# Revit family: ВКДВ_К2
name_source: partatom
category: Оборудование
units: mm (PartAtom-declared; Revit-internal decimal feet)

## family parameters
Всегда вертикально = Да
Классификация = Нет
На основе рабочей плоскости = Нет
Общий = Нет
При загрузке вырезать с полостями = Нет
Размер круглого соединителя = Использовать диаметр
Тип детали = Нормальный
Точка принадлежности помещению = Нет

## types (36) — shared parameters
00_20_Manufacturer = Вентс
00_20_Name = Даховий вентилятор димовидалення
Grid Material = Условный материал-отделка
Load Classification = HVAC
Maintenance zone material = <По категории>
Number of Fase = 3
Voltage = 400 В
zero-valued in all types: Отметка по умолчанию

## per-type parameters (varying)
| type | A | B | C | Casing Material | H | Maximum Air Flow | Power | R | h | h1 | h2 | Вес | Ш | Ш1 | Ш2 | Ш3 | ш | ш1 |
| ВКДВ-К2-710-4Д/11-K | 1180 мм | 980 мм | 1267 мм | <По категории> | 1264 мм | 7800.0 л/с | 11000 В·А | 440 мм | 421 мм | 246 мм | 381 мм | 342 кг | 1144 мм | 572 мм | 173 мм | 196 мм | 1012 мм | 506 мм |
| ВКДВ-К2-800-6Д/4-K | 1180 мм | 980 мм | 1311 мм | <По категории> | 1237 мм | 6950.0 л/с | 4000 В·А | 440 мм | 412 мм | 293 мм | 403 мм | 311 кг | 1209 мм | 605 мм | 216 мм | 243 мм | 1051 мм | 526 мм |
| ВКДВ-К2-1120-8Д/15-K | 1640 мм | 1340 мм | 1876 мм | <По категории> | 1866 мм | 17500.0 л/с | 15000 В·А | 600 мм | 622 мм | 415 мм | 583 мм | 911 кг | 1750 мм | 875 мм | 320 мм | 365 мм | 1550 мм | 775 мм |
| ВКДВ-К2-630-8Д/0,75-K | 1010 мм | 750 мм | 1121 мм | <По категории> | 1060 мм | 2500.0 л/с | 750 В·А | 400 мм | 353 мм | 265 мм | 327 мм | 200 кг | 980 мм | 490 мм | 190 мм | 215 мм | 920 мм | 460 мм |
| ВКДВ-К2-630-4Д/5,5-K | 1010 мм | 750 мм | 1121 мм | <По категории> | 1060 мм | 5200.0 л/с | 5500 В·А | 400 мм | 353 мм | 265 мм | 327 мм | 225 кг | 980 мм | 490 мм | 190 мм | 215 мм | 920 мм | 460 мм |
| ВКДВ-К2-710-8Д/1,1-K | 1180 мм | 980 мм | 1257 мм | <По категории> | 1105 мм | 3600.0 л/с | 1100 В·А | 440 мм | 368 мм | 287 мм | 381 мм | 231 кг | 1144 мм | 572 мм | 209 мм | 237 мм | 1012 мм | 506 мм |
| ВКДВ-К2-710-6Д/2,2-K | 1180 мм | 980 мм | 1257 мм | <По категории> | 1105 мм | 4800.0 л/с | 2200 В·А | 440 мм | 368 мм | 287 мм | 381 мм | 238 кг | 1144 мм | 572 мм | 209 мм | 237 мм | 1012 мм | 506 мм |
| ВКДВ-К2-800-8Д/2,2-K | 1180 мм | 980 мм | 1311 мм | <По категории> | 1237 мм | 5300.0 л/с | 2200 В·А | 440 мм | 412 мм | 298 мм | 399 мм | 308 кг | 1196 мм | 598 мм | 219 мм | 248 мм | 1058 мм | 529 мм |
| ВКДВ-К2-800-4Д/15-K | 1180 мм | 980 мм | 1311 мм | <По категории> | 1387 мм | 10800.0 л/с | 15000 В·А | 440 мм | 462 мм | 302 мм | 406 мм | 385 кг | 1217 мм | 609 мм | 222 мм | 252 мм | 1077 мм | 539 мм |
| ВКДВ-К2-900-10Д/2,2-K | 1340 мм | 1050 мм | 1494 мм | <По категории> | 1297 мм | 6250.0 л/с | 2200 В·А | 440 мм | 432 мм | 370 мм | 464 мм | 374 кг | 1392 мм | 696 мм | 300 мм | 320 мм | 1230 мм | 615 мм |
| ВКДВ-К2-900-8Д/4-K | 1340 мм | 1050 мм | 1494 мм | <По категории> | 1448 мм | 7500.0 л/с | 4000 В·А | 440 мм | 483 мм | 330 мм | 464 мм | 435 кг | 1392 мм | 696 мм | 260 мм | 280 мм | 1200 мм | 600 мм |
| ВКДВ-К2-900-6Д/7,5-K | 1340 мм | 1050 мм | 1494 мм | <По категории> | 1448 мм | 10500.0 л/с | 7500 В·А | 440 мм | 483 мм | 350 мм | 464 мм | 434 кг | 1392 мм | 696 мм | 280 мм | 300 мм | 1250 мм | 625 мм |
| ВКДВ-К2-900-4Д/30-K | 1340 мм | 1050 мм | 1524 мм | <По категории> | 1600 мм | 15500.0 л/с | 30000 В·А | 440 мм | 533 мм | 380 мм | 472 мм | 597 кг | 1416 мм | 708 мм | 300 мм | 330 мм | 1280 мм | 640 мм |
| ВКДВ-К2-1000-10Д/3-K | 1550 мм | 1340 мм | 1686 мм | Металл, окрашенный, синий, матовый RAL 5007 | 1595 мм | 9000.0 л/с | 3000 В·А | 500 мм | 532 мм | 370 мм | 520 мм | 573 кг | 1561 мм | 781 мм | 300 мм | 320 мм | 1340 мм | 670 мм |
| ВКДВ-К2-1000-8Д/7,5-K | 1550 мм | 1340 мм | 1686 мм | Металл, окрашенный, синий, матовый RAL 5007 | 1595 мм | 10800.0 л/с | 7500 В·А | 440 мм | 532 мм | 350 мм | 520 мм | 557 кг | 1560 мм | 780 мм | 280 мм | 300 мм | 1400 мм | 700 мм |
| ВКДВ-К2-1000-6Д/15-K | 1550 мм | 1340 мм | 1686 мм | Металл, окрашенный, синий, матовый RAL 5007 | 1680 мм | 15000.0 л/с | 15000 В·А | 440 мм | 560 мм | 350 мм | 519 мм | 608 кг | 1556 мм | 778 мм | 278 мм | 300 мм | 1400 мм | 700 мм |
| ВКДВ-К2-1120-10Д/7,5-K | 1640 мм | 1340 мм | 1876 мм | <По категории> | 1829 мм | 13800.0 л/с | 7500 В·А | 600 мм | 610 мм | 415 мм | 583 мм | 834 кг | 1750 мм | 875 мм | 320 мм | 365 мм | 1550 мм | 775 мм |
| ВКДВ-К2-1120-8Д/11-K | 1640 мм | 1340 мм | 1876 мм | <По категории> | 1753 мм | 15000.0 л/с | 11000 В·А | 600 мм | 584 мм | 415 мм | 583 мм | 834 кг | 1750 мм | 875 мм | 320 мм | 365 мм | 1550 мм | 775 мм |
| ВКДВ-К2-630-6Д/1,5-K | 1010 мм | 750 мм | 1121 мм | <По категории> | 1060 мм | 3500.0 л/с | 1500 В·А | 400 мм | 353 мм | 265 мм | 327 мм | 202 кг | 980 мм | 490 мм | 190 мм | 215 мм | 920 мм | 460 мм |
| ВКДВ-К2-1120-6Д/22-K | 1640 мм | 1340 мм | 1876 мм | <По категории> | 1789 мм | 20800.0 л/с | 22000 В·А | 600 мм | 596 мм | 415 мм | 583 мм | 856 кг | 1750 мм | 875 мм | 320 мм | 365 мм | 1550 мм | 775 мм |
| ВКДВ-К2-1120-6Д/30-K | 1640 мм | 1340 мм | 1876 мм | <По категории> | 1956 мм | 23500.0 л/с | 30000 В·А | 600 мм | 652 мм | 415 мм | 583 мм | 962 кг | 1750 мм | 875 мм | 320 мм | 365 мм | 1550 мм | 775 мм |
| ВКДВ-К2-560-4Д/3-K | 1000 мм | 750 мм | 1094 мм | <По категории> | 991 мм | 3750.0 л/с | 3000 В·А | 400 мм | 330 мм | 265 мм | 327 мм | 163 кг | 980 мм | 490 мм | 190 мм | 215 мм | 920 мм | 460 мм |
| ВКДВ-К2-560-6Д/0,75-K | 1000 мм | 750 мм | 1082 мм | <По категории> | 921 мм | 2400.0 л/с | 750 В·А | 400 мм | 307 мм | 265 мм | 327 мм | 151 кг | 980 мм | 490 мм | 190 мм | 215 мм | 920 мм | 460 мм |
| ВКДВ-К2-560-8Д/0,37-K | 1000 мм | 750 мм | 1082 мм | <По категории> | 921 мм | 1800.0 л/с | 370 В·А | 440 мм | 307 мм | 265 мм | 327 мм | 148 кг | 980 мм | 490 мм | 190 мм | 215 мм | 920 мм | 460 мм |
| ВКДВ-К2-500-4Д/1,5-K | 830 мм | 640 мм | 950 мм | <По категории> | 888 мм | 2700.0 л/с | 1500 В·А | 330 мм | 296 мм | 230 мм | 273 мм | 128 кг | 820 мм | 410 мм | 158 мм | 180 мм | 760 мм | 380 мм |
| ВКДВ-К2-500-6Д/0,55-K | 830 мм | 640 мм | 950 мм | <По категории> | 888 мм | 1100.0 л/с | 550 В·А | 330 мм | 296 мм | 230 мм | 273 мм | 122 кг | 820 мм | 410 мм | 158 мм | 180 мм | 760 мм | 380 мм |
| ВКДВ-К2-500-8Д/0,25-K | 830 мм | 640 мм | 950 мм | <По категории> | 888 мм | 420.0 л/с | 250 В·А | 330 мм | 296 мм | 230 мм | 273 мм | 121 кг | 820 мм | 410 мм | 158 мм | 180 мм | 760 мм | 380 мм |
| ВКДВ-К2-450-2Д/7,5-K | 810 мм | 580 мм | 933 мм | <По категории> | 929 мм | 3800.0 л/с | 7500 В·А | 330 мм | 310 мм | 230 мм | 273 мм | 137 кг | 820 мм | 410 мм | 158 мм | 180 мм | 760 мм | 380 мм |
| ВКДВ-К2-450-4Д/1,1-K | 760 мм | 580 мм | 864 мм | <По категории> | 794 мм | 1875.0 л/с | 1100 В·А | 300 мм | 265 мм | 213 мм | 248 мм | 96 кг | 745 мм | 373 мм | 143 мм | 163 мм | 690 мм | 345 мм |
| ВКДВ-К2-450-6Д/0,25-K | 760 мм | 580 мм | 864 мм | <По категории> | 794 мм | 1100.0 л/с | 250 В·А | 300 мм | 265 мм | 213 мм | 248 мм | 92 кг | 745 мм | 373 мм | 143 мм | 163 мм | 690 мм | 345 мм |
| ВКДВ-К2-400-2Д/4-K | 760 мм | 580 мм | 880 мм | <По категории> | 897 мм | 2600.0 л/с | 4000 В·А | 300 мм | 299 мм | 221 мм | 261 мм | 112 кг | 782 мм | 391 мм | 150 мм | 171 мм | 724 мм | 362 мм |
| ВКДВ-К2-400-4Д/0,55-K | 760 мм | 580 мм | 866 мм | Металл, окрашенный, синий, матовый RAL 5007 | 772 мм | 1250.0 л/с | 550 В·А | 300 мм | 257 мм | 213 мм | 248 мм | 83 кг | 745 мм | 373 мм | 143 мм | 163 мм | 690 мм | 345 мм |
| ВКДВ-К2-400-6Д/0,25-K | 760 мм | 580 мм | 866 мм | <По категории> | 772 мм | 800.0 л/с | 250 В·А | 300 мм | 257 мм | 213 мм | 248 мм | 82 кг | 745 мм | 373 мм | 143 мм | 163 мм | 690 мм | 345 мм |
| ВКДВ-К2-355-2Д/2,2-K | 680 мм | 480 мм | 820 мм | <По категории> | 801 мм | 1875.0 л/с | 2200 В·А | 244 мм | 267 мм | 182 мм | 200 мм | 89 кг | 600 мм | 300 мм | 116 мм | 132 мм | 560 мм | 280 мм |
| ВКДВ-К2-355-4Д/0,25-K | 680 мм | 480 мм | 820 мм | <По категории> | 744 мм | 880.0 л/с | 250 В·А | 244 мм | 248 мм | 208 мм | 240 мм | 73 кг | 720 мм | 360 мм | 139 мм | 158 мм | 672 мм | 336 мм |
| ВКДВ-К2-315-2Д/1,1-K | 680 мм | 480 мм | 820 мм | <По категории> | 779 мм | 1300.0 л/с | 1100 В·А | 244 мм | 260 мм | 208 мм | 240 мм | 80 кг | 720 мм | 360 мм | 139 мм | 158 мм | 672 мм | 336 мм |

note: column(s) folded — value = type name in every type: 00_20_Type
